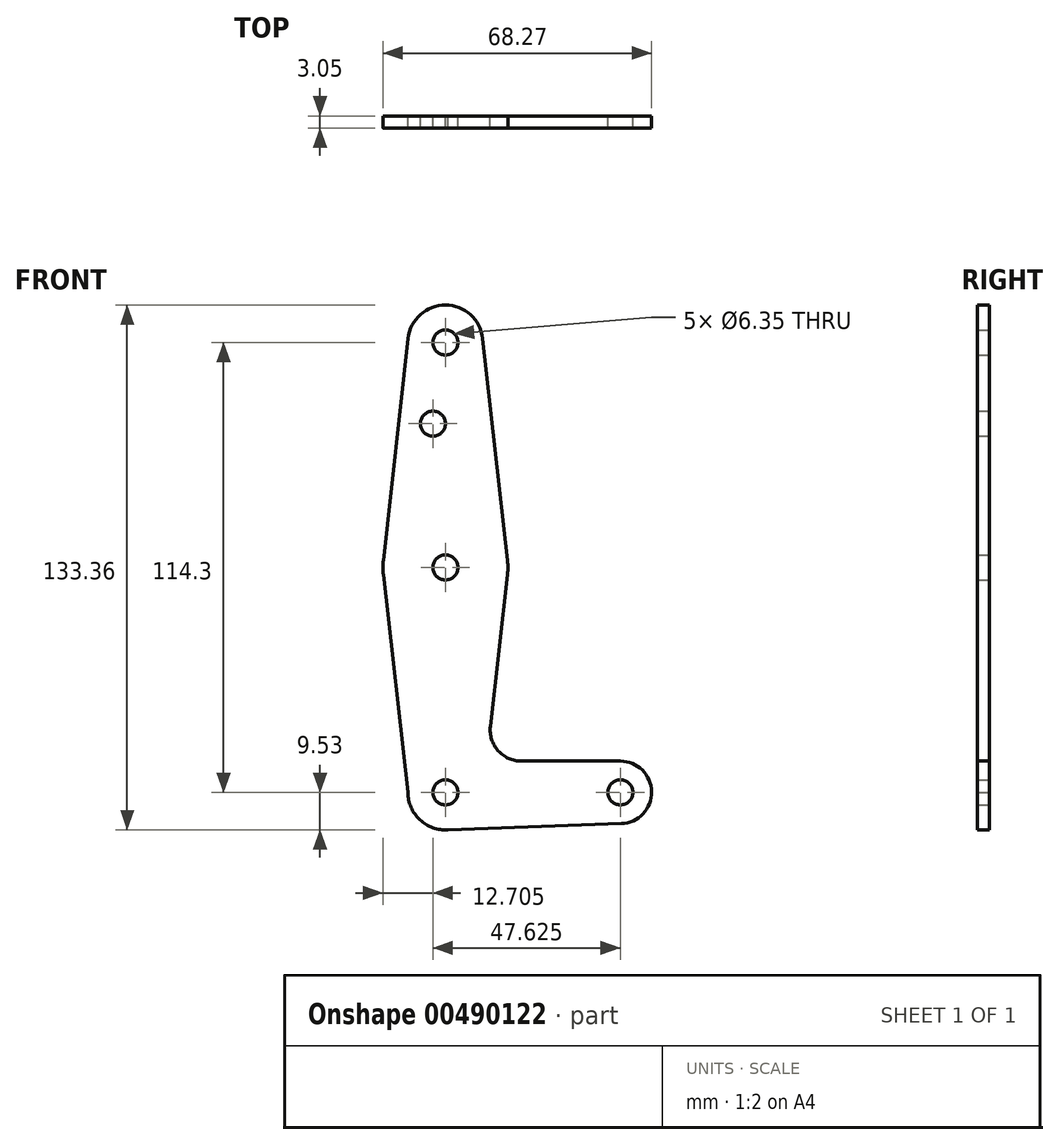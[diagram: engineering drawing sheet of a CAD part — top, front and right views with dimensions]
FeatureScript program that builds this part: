
annotation { "Feature Type Name" : "Feature", "Feature Type Description" : "" }
export const myFeature = defineFeature(function(context is Context, id is Id, definition is map)
    precondition{}
    {
        {
            var Q0;
            Q0=qCreatedBy(makeId("Front.planeOp"),FACE);
            var sketch = newSketch(context, id + "F0", { "sketchPlane" : qUnion([Q0])});
            skLineSegment(sketch, "E0", {"start": v(0, 0) * mm, "end": v(0, 114.3) * mm});
            skLineSegment(sketch, "E1", {"start": v(0, 0) * mm, "end": v(44.45, 0) * mm});
            skCircle(sketch, "E2", {"center": v(0, 114.3) * mm, "radius": 9.53 * mm});
            skCircle(sketch, "E3", {"center": v(0, 57.15) * mm, "radius": 15.88 * mm});
            skCircle(sketch, "E4", {"center": v(44.45, 0) * mm, "radius": 7.94 * mm});
            skCircle(sketch, "E5", {"center": v(0, 0) * mm, "radius": 9.53 * mm});
            skLineSegment(sketch, "E6", {"start": v(-9.47, 115.36) * mm, "end": v(-15.78, 58.91) * mm});
            skLineSegment(sketch, "E7", {"start": v(0, -9.53) * mm, "end": v(44.73, -7.93) * mm});
            skLineSegment(sketch, "E8", {"start": v(44.45, 7.94) * mm, "end": v(19.32, 7.94) * mm});
            skLineSegment(sketch, "E9", {"start": v(11.42, 16.78) * mm, "end": v(15.77, 55.37) * mm});
            skLineSegment(sketch, "E10", {"start": v(15.78, 58.91) * mm, "end": v(9.47, 115.36) * mm});
            skLineSegment(sketch, "E11", {"start": v(-9.53, 0) * mm, "end": v(-15.77, 55.37) * mm});
            skCircle(sketch, "E12", {"center": v(0, 114.3) * mm, "radius": 3.18 * mm});
            skCircle(sketch, "E13", {"center": v(0, 57.15) * mm, "radius": 3.18 * mm});
            skCircle(sketch, "E14", {"center": v(0, 0) * mm, "radius": 3.18 * mm});
            skCircle(sketch, "E15", {"center": v(44.45, 0) * mm, "radius": 3.18 * mm});
            skCircle(sketch, "E16", {"center": v(-3.17, 93.68) * mm, "radius": 3.18 * mm});
            skArc(sketch, "E17.filletArc", {"start": v(11.42, 16.78) * mm, "mid": v(13.4, 10.6) * mm, "end": v(19.32, 7.94) * mm});
            skSolve(sketch);
        }
        {
            var Q0;
            Q0 = qSketchRegion(id + "F0", true);
            var Q1;
            {var subQ0=sQuery(id+"F0.wireOp",EDGE,"E14");var subQ1=sQuery(id+"F0.wireOp",EDGE,"E0");var subQ2=makeQuery(id+"F0.imprint","INTERSECT",VERTEX,{"derivedFrom":[subQ1,subQ0]});Q1=makeQuery(id+"F0.imprint","IMPRINT",FACE,{"disambiguationData":[TD([[makeQuery(id+"F0.imprint","IMPRINT",EDGE,{"disambiguationData":[TD([[subQ2,-1.0]])],"derivedFrom":subQ1}),-1.0]])]});}
            extrude(context, id + "F1", {"entities" : qUnion([Q0, Q1]), "depth" : 3.05 * mm});
        }
    });
